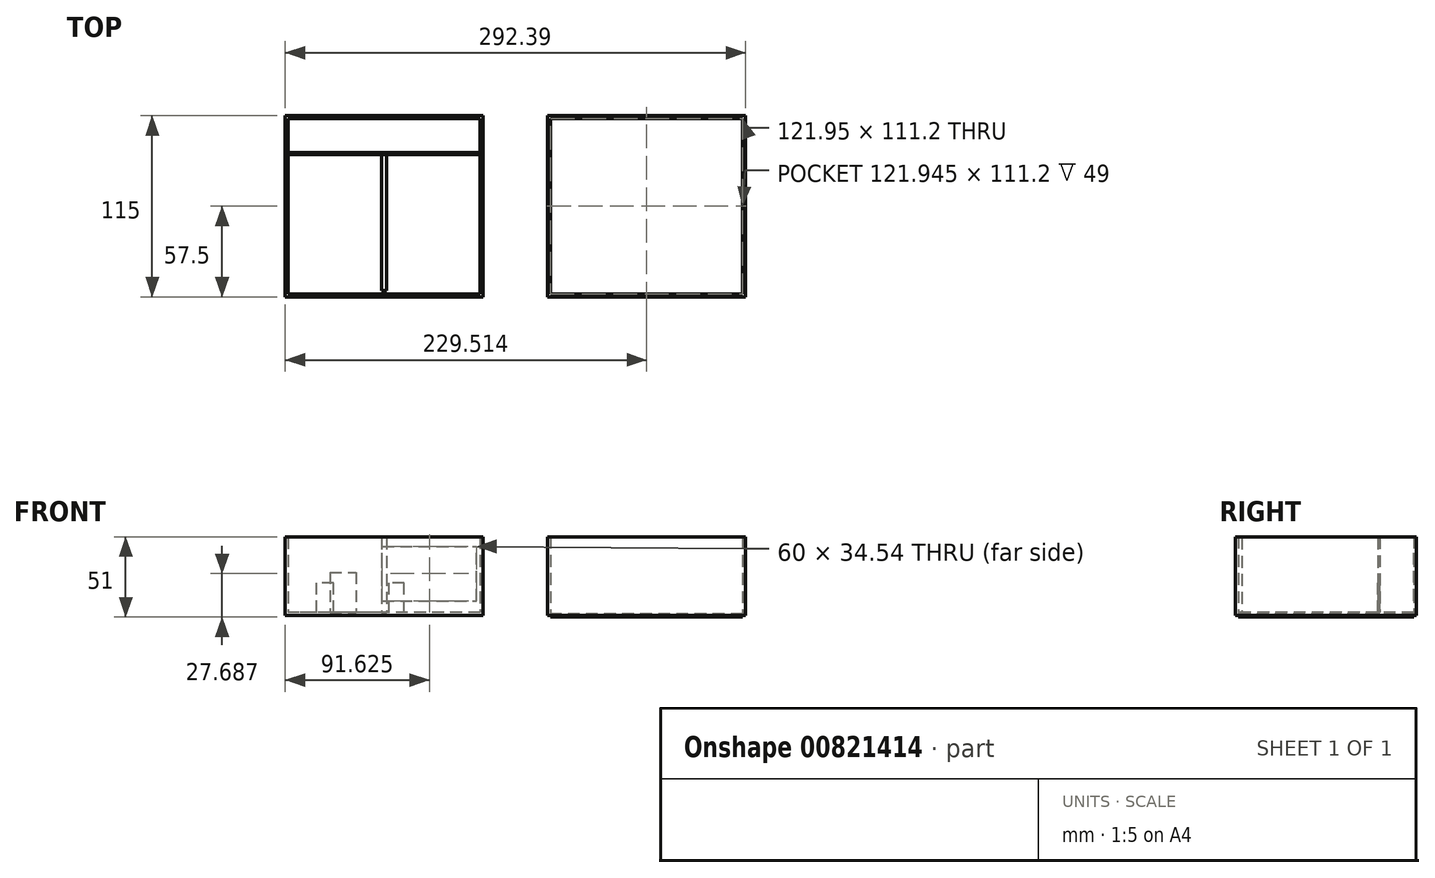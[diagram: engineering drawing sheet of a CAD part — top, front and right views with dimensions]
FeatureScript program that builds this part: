
annotation { "Feature Type Name" : "Feature", "Feature Type Description" : "" }
export const myFeature = defineFeature(function(context is Context, id is Id, definition is map)
    precondition{}
    {
        {
            var Q0;
            Q0=qCreatedBy(makeId("Top.planeOp"),FACE);
            var sketch = newSketch(context, id + "F0", { "sketchPlane" : qUnion([Q0])});
            skLineSegment(sketch, "E0.bottom", {"start": v(62.87, 57.5) * mm, "end": v(-62.87, 57.5) * mm});
            skLineSegment(sketch, "E0.top", {"start": v(62.87, -57.5) * mm, "end": v(-62.87, -57.5) * mm});
            skLineSegment(sketch, "E0.left", {"start": v(62.87, 57.5) * mm, "end": v(62.87, -57.5) * mm});
            skLineSegment(sketch, "E0.right", {"start": v(-62.87, 57.5) * mm, "end": v(-62.87, -57.5) * mm});
            skPoint(sketch, "E0.middle", {"position": v(0, 0) * mm});
            skLineSegment(sketch, "E1.0", {"start": v(60.97, 55.6) * mm, "end": v(-60.97, 55.6) * mm});
            skLineSegment(sketch, "E1.1", {"start": v(60.97, 55.6) * mm, "end": v(60.97, -55.6) * mm});
            skLineSegment(sketch, "E1.2", {"start": v(60.97, -55.6) * mm, "end": v(-60.97, -55.6) * mm});
            skLineSegment(sketch, "E1.3", {"start": v(-60.97, 55.6) * mm, "end": v(-60.97, -55.6) * mm});
            skLineSegment(sketch, "E2.bottom", {"start": v(229.52, 57.5) * mm, "end": v(103.77, 57.5) * mm});
            skLineSegment(sketch, "E2.top", {"start": v(229.52, -57.5) * mm, "end": v(103.77, -57.5) * mm});
            skLineSegment(sketch, "E2.left", {"start": v(229.52, 57.5) * mm, "end": v(229.52, -57.5) * mm});
            skLineSegment(sketch, "E2.right", {"start": v(103.77, 57.5) * mm, "end": v(103.77, -57.5) * mm});
            skPoint(sketch, "E2.middle", {"position": v(166.64, 0) * mm});
            skLineSegment(sketch, "E3.0", {"start": v(105.67, 55.6) * mm, "end": v(105.67, -55.6) * mm});
            skLineSegment(sketch, "E3.1", {"start": v(227.62, 55.6) * mm, "end": v(105.67, 55.6) * mm});
            skLineSegment(sketch, "E3.2", {"start": v(227.62, 55.6) * mm, "end": v(227.62, -55.6) * mm});
            skLineSegment(sketch, "E3.3", {"start": v(227.62, -55.6) * mm, "end": v(105.67, -55.6) * mm});
            skSolve(sketch);
        }
        {
            var Q0;
            Q0=makeQuery(id+"F0.imprint","IMPRINT",FACE,{"disambiguationData":[TD([[makeQuery(id+"F0.imprint","IMPRINT",EDGE,{"derivedFrom":sQuery(id+"F0.wireOp",EDGE,"E0.bottom")}),1.0]])]});
            extrude(context, id + "F1", {"entities" : qUnion([Q0]), "depth" : 50 * mm, "offsetDistance" : 25 * mm});
        }
        {
            var Q0;
            Q0=makeQuery(id+"F0.imprint","IMPRINT",FACE,{"disambiguationData":[TD([[makeQuery(id+"F0.imprint","IMPRINT",EDGE,{"derivedFrom":sQuery(id+"F0.wireOp",EDGE,"E1.0")}),1.0]])]});
            var Q1;
            Q1=makeQuery(id+"F0.imprint","IMPRINT",FACE,{"disambiguationData":[TD([[makeQuery(id+"F0.imprint","IMPRINT",EDGE,{"derivedFrom":sQuery(id+"F0.wireOp",EDGE,"E0.bottom")}),1.0]])]});
            extrude(context, id + "F2", {"entities" : qUnion([Q0, Q1]), "operationType" : NewBodyOperationType.ADD, "depth" : 2 * mm, "offsetDistance" : 25 * mm});
        }
        {
            var Q0;
            Q0=makeQuery(id+"F0.imprint","IMPRINT",FACE,{"disambiguationData":[TD([[makeQuery(id+"F0.imprint","IMPRINT",EDGE,{"derivedFrom":sQuery(id+"F0.wireOp",EDGE,"E2.bottom")}),1.0]])]});
            extrude(context, id + "F3", {"entities" : qUnion([Q0]), "depth" : 50 * mm, "offsetDistance" : 25 * mm});
        }
        {
            var Q0;
            Q0=makeQuery(id+"F0.imprint","IMPRINT",FACE,{"disambiguationData":[TD([[makeQuery(id+"F0.imprint","IMPRINT",EDGE,{"derivedFrom":sQuery(id+"F0.wireOp",EDGE,"E3.0")}),1.0]])]});
            extrude(context, id + "F4", {"entities" : qUnion([Q0]), "operationType" : NewBodyOperationType.ADD, "endBound" : BoundingType.SYMMETRIC, "depth" : 2 * mm, "offsetDistance" : 25 * mm});
        }
        {
            var Q0;
            Q0=makeQuery(id+"F1.opExtrude","SWEPT_FACE",FACE,{"disambiguationData":[OSD([sQuery(id+"F0.wireOp",EDGE,"E0.bottom")])]});
            var sketch = newSketch(context, id + "F5", { "sketchPlane" : qUnion([Q0])});
            skLineSegment(sketch, "E4.bottom", {"start": v(-58.75, 43.95) * mm, "end": v(1.25, 43.95) * mm});
            skLineSegment(sketch, "E4.top", {"start": v(-58.75, 9.42) * mm, "end": v(1.25, 9.42) * mm});
            skLineSegment(sketch, "E4.left", {"start": v(-58.75, 43.95) * mm, "end": v(-58.75, 9.42) * mm});
            skLineSegment(sketch, "E4.right", {"start": v(1.25, 43.95) * mm, "end": v(1.25, 9.42) * mm});
            skLineSegment(sketch, "E5.bottom", {"start": v(17.9, 2) * mm, "end": v(34.5, 2) * mm});
            skLineSegment(sketch, "E5.top", {"start": v(17.9, 27.52) * mm, "end": v(34.5, 27.52) * mm});
            skLineSegment(sketch, "E5.left", {"start": v(17.9, 2) * mm, "end": v(17.9, 27.52) * mm});
            skLineSegment(sketch, "E5.right", {"start": v(34.5, 2) * mm, "end": v(34.5, 27.52) * mm});
            skSolve(sketch);
        }
        {
            var Q0;
            Q0 = qSketchRegion(id + "F5", true);
            extrude(context, id + "F6", {"entities" : qUnion([Q0]), "endBound" : BoundingType.SYMMETRIC, "oppositeDirection" : true, "depth" : 25 * mm, "offsetDistance" : 25 * mm});
        }
        {
            var Q0;
            Q0=makeQuery(id+"F6.opExtrude","SWEPT_BODY",BODY,{"disambiguationData":[OSD([sQuery(id+"F5.wireOp",EDGE,"E4.bottom"),sQuery(id+"F5.wireOp",EDGE,"E4.top"),sQuery(id+"F5.wireOp",EDGE,"E4.left"),sQuery(id+"F5.wireOp",EDGE,"E4.right")])]});
            var Q1;
            Q1=makeQuery(id+"F6.opExtrude","SWEPT_BODY",BODY,{"disambiguationData":[OSD([sQuery(id+"F5.wireOp",EDGE,"E5.bottom"),sQuery(id+"F5.wireOp",EDGE,"E5.top"),sQuery(id+"F5.wireOp",EDGE,"E5.left"),sQuery(id+"F5.wireOp",EDGE,"E5.right")])]});
            var Q2;
            Q2=makeQuery(id+"F1.opExtrude","SWEPT_BODY",BODY,{"disambiguationData":[OSD([sQuery(id+"F0.wireOp",EDGE,"E0.bottom"),sQuery(id+"F0.wireOp",EDGE,"E0.top"),sQuery(id+"F0.wireOp",EDGE,"E0.left"),sQuery(id+"F0.wireOp",EDGE,"E0.right"),sQuery(id+"F0.wireOp",EDGE,"E1.0"),sQuery(id+"F0.wireOp",EDGE,"E1.1"),sQuery(id+"F0.wireOp",EDGE,"E1.2"),sQuery(id+"F0.wireOp",EDGE,"E1.3")])]});
            booleanBodies(context, id + "F7", {"operationType" : BooleanOperationType.SUBTRACTION, "tools" : qUnion([Q0, Q1]), "targets" : qUnion([Q2])});
        }
        {
            var Q0;
            Q0=makeQuery(id+"F7.opBoolean","MERGE",FACE,{"derivedFrom":[makeQuery(id+"F2.opExtrude","CAP_FACE",FACE,{"disambiguationData":[OSD([sQuery(id+"F0.wireOp",EDGE,"E0.bottom"),sQuery(id+"F0.wireOp",EDGE,"E0.top"),sQuery(id+"F0.wireOp",EDGE,"E0.left"),sQuery(id+"F0.wireOp",EDGE,"E0.right")])],"isStart":false}),makeQuery(id+"F6.opExtrude","SWEPT_FACE",FACE,{"disambiguationData":[OSD([sQuery(id+"F5.wireOp",EDGE,"E5.bottom")])]})]});
            var sketch = newSketch(context, id + "F8", { "sketchPlane" : qUnion([Q0])});
            skLineSegment(sketch, "E6.bottom", {"start": v(60.97, 34.22) * mm, "end": v(-60.97, 34.22) * mm});
            skLineSegment(sketch, "E6.top", {"start": v(60.97, 32.9) * mm, "end": v(-60.97, 32.9) * mm});
            skLineSegment(sketch, "E6.left", {"start": v(60.97, 34.22) * mm, "end": v(60.97, 32.9) * mm});
            skLineSegment(sketch, "E6.right", {"start": v(-60.97, 34.22) * mm, "end": v(-60.97, 32.9) * mm});
            skSolve(sketch);
        }
        {
            var Q0;
            Q0=makeQuery(id+"F8.imprint","IMPRINT",FACE,{"disambiguationData":[TD([[makeQuery(id+"F8.imprint","IMPRINT",EDGE,{"derivedFrom":sQuery(id+"F8.wireOp",EDGE,"E6.bottom")}),1.0]])]});
            extrude(context, id + "F9", {"entities" : qUnion([Q0]), "operationType" : NewBodyOperationType.ADD, "depth" : 47.8 * mm, "offsetDistance" : 25 * mm});
        }
        {
            var Q0;
            Q0=makeQuery(id+"F9.opExtrude","SWEPT_FACE",FACE,{"disambiguationData":[OSD([sQuery(id+"F8.wireOp",EDGE,"E6.top")])]});
            var sketch = newSketch(context, id + "F10", { "sketchPlane" : qUnion([Q0])});
            skLineSegment(sketch, "E7.bottom", {"start": v(-42.8, 20.66) * mm, "end": v(-32, 20.66) * mm});
            skLineSegment(sketch, "E7.top", {"start": v(-42.8, 2) * mm, "end": v(-32, 2) * mm});
            skLineSegment(sketch, "E7.left", {"start": v(-42.8, 20.66) * mm, "end": v(-42.8, 2) * mm});
            skLineSegment(sketch, "E7.right", {"start": v(-32, 20.66) * mm, "end": v(-32, 2) * mm});
            skLineSegment(sketch, "E8.bottom", {"start": v(3.04, 20.6) * mm, "end": v(12.75, 20.6) * mm});
            skLineSegment(sketch, "E8.top", {"start": v(3.04, 2) * mm, "end": v(12.75, 2) * mm});
            skLineSegment(sketch, "E8.left", {"start": v(3.04, 20.6) * mm, "end": v(3.04, 2) * mm});
            skLineSegment(sketch, "E8.right", {"start": v(12.75, 20.6) * mm, "end": v(12.75, 2) * mm});
            skSolve(sketch);
        }
        {
            var Q0;
            Q0=makeQuery(id+"F10.imprint","IMPRINT",FACE,{"disambiguationData":[TD([[makeQuery(id+"F10.imprint","IMPRINT",EDGE,{"derivedFrom":sQuery(id+"F10.wireOp",EDGE,"E7.bottom")}),-1.0]])]});
            var Q1;
            Q1=makeQuery(id+"F10.imprint","IMPRINT",FACE,{"disambiguationData":[TD([[makeQuery(id+"F10.imprint","IMPRINT",EDGE,{"derivedFrom":sQuery(id+"F10.wireOp",EDGE,"E8.bottom")}),-1.0]])]});
            extrude(context, id + "F11", {"entities" : qUnion([Q0, Q1]), "endBound" : BoundingType.SYMMETRIC, "depth" : 25 * mm, "offsetDistance" : 25 * mm});
        }
        {
            var Q0;
            Q0=makeQuery(id+"F11.opExtrude","SWEPT_BODY",BODY,{"disambiguationData":[OSD([sQuery(id+"F10.wireOp",EDGE,"E7.bottom"),sQuery(id+"F10.wireOp",EDGE,"E7.top"),sQuery(id+"F10.wireOp",EDGE,"E7.left"),sQuery(id+"F10.wireOp",EDGE,"E7.right")])]});
            var Q1;
            Q1=makeQuery(id+"F11.opExtrude","SWEPT_BODY",BODY,{"disambiguationData":[OSD([sQuery(id+"F10.wireOp",EDGE,"E8.bottom"),sQuery(id+"F10.wireOp",EDGE,"E8.top"),sQuery(id+"F10.wireOp",EDGE,"E8.left"),sQuery(id+"F10.wireOp",EDGE,"E8.right")])]});
            var Q2;
            Q2=makeQuery(id+"F1.opExtrude","SWEPT_BODY",BODY,{"disambiguationData":[OSD([sQuery(id+"F0.wireOp",EDGE,"E0.bottom"),sQuery(id+"F0.wireOp",EDGE,"E0.top"),sQuery(id+"F0.wireOp",EDGE,"E0.left"),sQuery(id+"F0.wireOp",EDGE,"E0.right"),sQuery(id+"F0.wireOp",EDGE,"E1.0"),sQuery(id+"F0.wireOp",EDGE,"E1.1"),sQuery(id+"F0.wireOp",EDGE,"E1.2"),sQuery(id+"F0.wireOp",EDGE,"E1.3")])]});
            booleanBodies(context, id + "F12", {"operationType" : BooleanOperationType.SUBTRACTION, "tools" : qUnion([Q0, Q1]), "targets" : qUnion([Q2])});
        }
        {
            var Q0;
            {var subQ2=sQuery(id+"F0.wireOp",EDGE,"E0.bottom");var subQ3=makeQuery(id+"F7.opBoolean","MERGE",FACE,{"derivedFrom":[makeQuery(id+"F2.opExtrude","CAP_FACE",FACE,{"disambiguationData":[OSD([subQ2,sQuery(id+"F0.wireOp",EDGE,"E0.top"),sQuery(id+"F0.wireOp",EDGE,"E0.left"),sQuery(id+"F0.wireOp",EDGE,"E0.right")])],"isStart":false}),makeQuery(id+"F6.opExtrude","SWEPT_FACE",FACE,{"disambiguationData":[OSD([sQuery(id+"F5.wireOp",EDGE,"E5.bottom")])]})]});Q0=makeQuery(id+"F12.opBoolean","MERGE",FACE,{"derivedFrom":[makeQuery(id+"F9.boolean.opBoolean","SPLIT",FACE,{"disambiguationData":[TD([makeQuery(id+"F1.opExtrude","SWEPT_FACE",FACE,{"disambiguationData":[OSD([sQuery(id+"F0.wireOp",EDGE,"E1.2")])]})])],"derivedFrom":subQ3}),makeQuery(id+"F9.boolean.opBoolean","SPLIT",FACE,{"disambiguationData":[TD([makeQuery(id+"F1.opExtrude","SWEPT_FACE",FACE,{"disambiguationData":[OSD([subQ2])]})])],"derivedFrom":subQ3}),makeQuery(id+"F11.opExtrude","SWEPT_FACE",FACE,{"disambiguationData":[OSD([sQuery(id+"F10.wireOp",EDGE,"E7.top")])]}),makeQuery(id+"F11.opExtrude","SWEPT_FACE",FACE,{"disambiguationData":[OSD([sQuery(id+"F10.wireOp",EDGE,"E8.top")])]})]});}
            var sketch = newSketch(context, id + "F13", { "sketchPlane" : qUnion([Q0])});
            skLineSegment(sketch, "E9.bottom", {"start": v(-1.52, 32.9) * mm, "end": v(1.5, 32.9) * mm});
            skLineSegment(sketch, "E9.top", {"start": v(-1.52, -53.6) * mm, "end": v(1.5, -53.6) * mm});
            skLineSegment(sketch, "E9.left", {"start": v(-1.52, 32.9) * mm, "end": v(-1.52, -53.6) * mm});
            skLineSegment(sketch, "E9.right", {"start": v(1.5, 32.9) * mm, "end": v(1.5, -53.6) * mm});
            skSolve(sketch);
        }
        {
            var Q0;
            Q0 = qSketchRegion(id + "F13", true);
            extrude(context, id + "F14", {"entities" : qUnion([Q0]), "operationType" : NewBodyOperationType.ADD, "depth" : 47.4 * mm, "offsetDistance" : 25 * mm});
        }
        {
            var Q0;
            Q0=makeQuery(id+"F4.opExtrude","CAP_FACE",FACE,{"disambiguationData":[OSD([sQuery(id+"F0.wireOp",EDGE,"E3.0"),sQuery(id+"F0.wireOp",EDGE,"E3.1"),sQuery(id+"F0.wireOp",EDGE,"E3.2"),sQuery(id+"F0.wireOp",EDGE,"E3.3")])],"isStart":false});
            var sketch = newSketch(context, id + "F15", { "sketchPlane" : qUnion([Q0])});
            skLineSegment(sketch, "E10.bottom", {"start": v(174.85, 0) * mm, "end": v(225.62, 0) * mm});
            skLineSegment(sketch, "E10.top", {"start": v(174.85, -53.6) * mm, "end": v(225.62, -53.6) * mm});
            skLineSegment(sketch, "E10.left", {"start": v(174.85, 0) * mm, "end": v(174.85, -53.6) * mm});
            skLineSegment(sketch, "E10.right", {"start": v(225.62, 0) * mm, "end": v(225.62, -53.6) * mm});
            skSolve(sketch);
        }
        {
            var Q0;
            Q0=sQuery(id+"F15.wireOp",EDGE,"E10.bottom");
            var Q1;
            Q1=sQuery(id+"F15.wireOp",EDGE,"E10.left");
            var Q2;
            Q2=sQuery(id+"F15.wireOp",EDGE,"E10.right");
            var Q3;
            Q3=sQuery(id+"F15.wireOp",EDGE,"E10.top");
            extrude(context, id + "F16", {"bodyType" : ToolBodyType.SURFACE, "surfaceEntities" : qUnion([Q0, Q1, Q2, Q3]), "depth" : 50 * mm, "offsetDistance" : 25 * mm});
        }
    });
